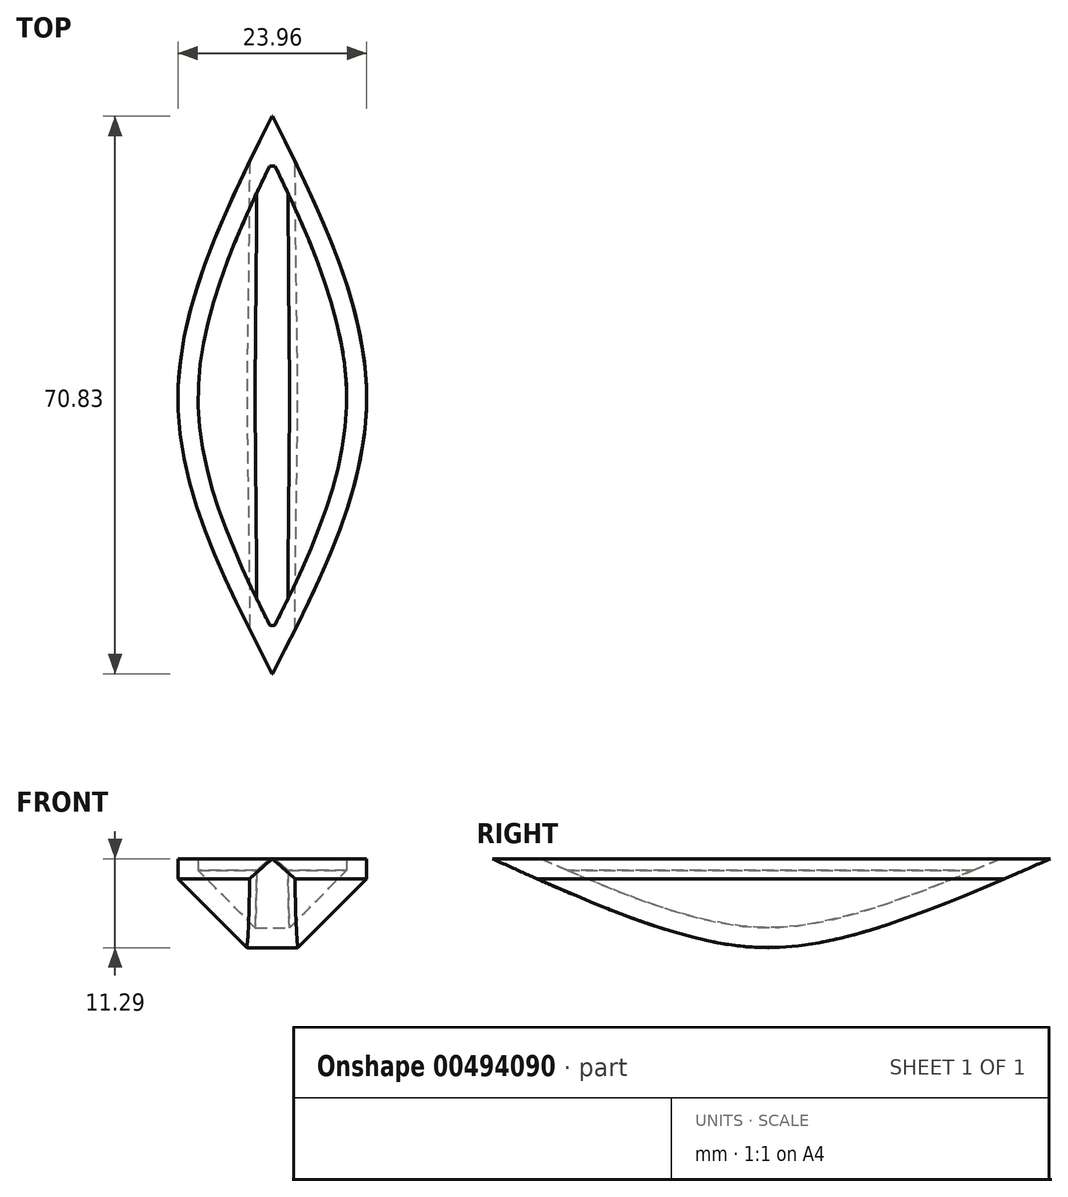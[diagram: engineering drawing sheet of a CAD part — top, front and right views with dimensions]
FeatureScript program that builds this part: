
annotation { "Feature Type Name" : "Feature", "Feature Type Description" : "" }
export const myFeature = defineFeature(function(context is Context, id is Id, definition is map)
    precondition{}
    {
        {
            var Q0;
            Q0=qCreatedBy(makeId("Top.planeOp"),FACE);
            var sketch = newSketch(context, id + "F0", { "sketchPlane" : qUnion([Q0])});
            skFitSpline(sketch, "E0", {"points": [v(0, 36.16) * mm, v(-11.98, 0) * mm, v(0, -34.8) * mm], "startDerivative": vector(-35.84, -72.09) * mm, "endDerivative": vector(36.04, -69.84) * mm});
            skLineSegment(sketch, "E1", {"start": v(0, 36.16) * mm, "end": v(0, -34.8) * mm});
            skFitSpline(sketch, "E2.MirrorCS", {"points": [v(0, 36.16) * mm, v(11.98, 0) * mm, v(0, -34.8) * mm], "startDerivative": vector(35.84, -72.09) * mm, "endDerivative": vector(-36.04, -69.84) * mm});
            skSolve(sketch);
        }
        {
            var Q0;
            Q0 = qSketchRegion(id + "F0", true);
            extrude(context, id + "F1", {"entities" : qUnion([Q0]), "depth" : 15.24 * mm});
        }
        {
            var Q0;
            Q0=makeQuery(id+"F1.opExtrude","CAP_EDGE",EDGE,{"disambiguationData":[OSD([sQuery(id+"F0.wireOp",EDGE,"E2.MirrorCS")])],"isStart":true});
            chamfer(context, id + "F2", {"entities" : qUnion([Q0]), "width" : 12.7 * mm, "tangentPropagation" : true});
        }
        {
            var Q0;
            Q0=makeQuery(id+"F1.opExtrude","CAP_EDGE",EDGE,{"disambiguationData":[OSD([sQuery(id+"F0.wireOp",EDGE,"E0")])],"isStart":true});
            chamfer(context, id + "F3", {"entities" : qUnion([Q0]), "width" : 12.7 * mm, "tangentPropagation" : true});
        }
        {
            var Q0;
            Q0=makeQuery(id+"F3.opChamfer","BLEND_EDGE",EDGE,{"blendedFrom":[makeQuery(id+"F1.opExtrude","CAP_EDGE",EDGE,{"disambiguationData":[OSD([sQuery(id+"F0.wireOp",EDGE,"E0")])],"isStart":true}),makeQuery(id+"F2.opChamfer","BLEND_FACE",FACE,{"disambiguationData":[OSD([sQuery(id+"F0.wireOp",EDGE,"E2.MirrorCS")])]})],"blendedInto":[makeQuery(id+"F2.opChamfer","BLEND_FACE",FACE,{"disambiguationData":[OSD([sQuery(id+"F0.wireOp",EDGE,"E2.MirrorCS")])]})]});
            chamfer(context, id + "F4", {"entities" : qUnion([Q0]), "width" : 4.57 * mm, "tangentPropagation" : true});
        }
        {
            var Q0;
            Q0=qCreatedBy(makeId("Right.planeOp"),FACE);
            var sketch = newSketch(context, id + "F5", { "sketchPlane" : qUnion([Q0])});
            skLineSegment(sketch, "E3", {"start": v(23.5, 3.16) * mm, "end": v(-24.64, 3.16) * mm});
            skLineSegment(sketch, "E4", {"start": v(-24.64, 3.16) * mm, "end": v(-24.64, -2.94) * mm});
            skLineSegment(sketch, "E5", {"start": v(-24.64, -2.94) * mm, "end": v(23.5, -2.94) * mm});
            skLineSegment(sketch, "E6", {"start": v(23.5, -2.94) * mm, "end": v(23.5, 3.16) * mm});
            skSolve(sketch);
        }
        {
            var Q0;
            Q0 = qSketchRegion(id + "F5", true);
            extrude(context, id + "F6", {"entities" : qUnion([Q0]), "operationType" : NewBodyOperationType.REMOVE, "oppositeDirection" : true, "depth" : 25.4 * mm});
        }
        {
            var Q0;
            Q0=makeQuery(id+"F1.opExtrude","CAP_FACE",FACE,{"disambiguationData":[OSD([sQuery(id+"F0.wireOp",EDGE,"E0"),sQuery(id+"F0.wireOp",EDGE,"E2.MirrorCS")])],"isStart":false});
            shell(context, id + "F7", {"entities" : qUnion([Q0]), "thickness" : 2.54 * mm});
        }
    });
